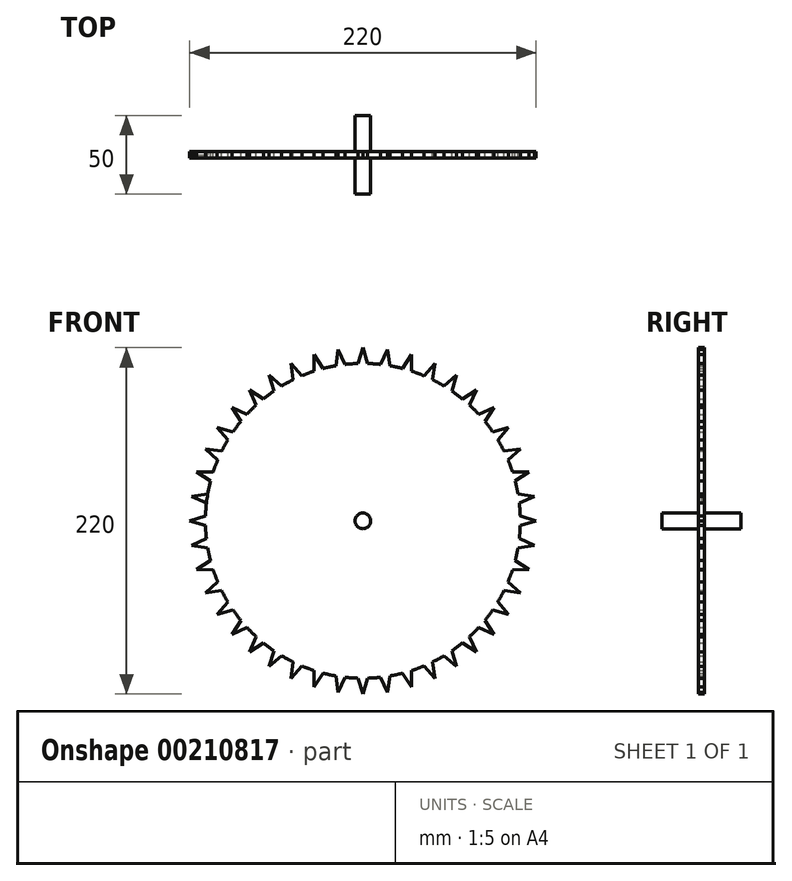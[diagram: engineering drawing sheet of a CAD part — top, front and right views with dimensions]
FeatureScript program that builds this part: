
annotation { "Feature Type Name" : "Feature", "Feature Type Description" : "" }
export const myFeature = defineFeature(function(context is Context, id is Id, definition is map)
    precondition{}
    {
        {
            var Q0;
            Q0=qCreatedBy(makeId("Front.planeOp"),FACE);
            var sketch = newSketch(context, id + "F0", { "sketchPlane" : qUnion([Q0])});
            skArc(sketch, "E0", {"start": v(135, 67.77) * mm, "mid": v(133.09, 71.44) * mm, "end": v(131.03, 75.03) * mm});
            skCircle(sketch, "E1", {"center": v(45.32, 23.52) * mm, "radius": 5 * mm});
            skCircle(sketch, "E2", {"center": v(45.32, 23.52) * mm, "radius": 110 * mm});
            skLineSegment(sketch, "E3", {"start": v(45.32, 123.52) * mm, "end": v(45.32, 133.52) * mm, "construction": true});
            skLineSegment(sketch, "E4", {"start": v(45.32, 133.52) * mm, "end": v(48.32, 123.47) * mm});
            skLineSegment(sketch, "E5.MirrorCS", {"start": v(45.32, 133.52) * mm, "end": v(42.32, 123.47) * mm});
            skLineSegment(sketch, "E6.1.0", {"start": v(59.55, 122.5) * mm, "end": v(60.98, 132.4) * mm, "construction": true});
            skLineSegment(sketch, "E6.1.1", {"start": v(60.98, 132.4) * mm, "end": v(56.58, 122.88) * mm});
            skLineSegment(sketch, "E6.1.2", {"start": v(60.98, 132.4) * mm, "end": v(62.52, 122.03) * mm});
            skLineSegment(sketch, "E6.2.0", {"start": v(73.5, 119.47) * mm, "end": v(76.31, 129.06) * mm, "construction": true});
            skLineSegment(sketch, "E6.2.1", {"start": v(76.31, 129.06) * mm, "end": v(70.6, 120.27) * mm});
            skLineSegment(sketch, "E6.2.2", {"start": v(76.31, 129.06) * mm, "end": v(76.36, 118.58) * mm});
            skLineSegment(sketch, "E6.3.0", {"start": v(86.86, 114.48) * mm, "end": v(91.02, 123.58) * mm, "construction": true});
            skLineSegment(sketch, "E6.3.1", {"start": v(91.02, 123.58) * mm, "end": v(84.12, 115.69) * mm});
            skLineSegment(sketch, "E6.3.2", {"start": v(91.02, 123.58) * mm, "end": v(89.57, 113.2) * mm});
            skLineSegment(sketch, "E6.4.0", {"start": v(99.39, 107.64) * mm, "end": v(104.8, 116.06) * mm, "construction": true});
            skLineSegment(sketch, "E6.4.1", {"start": v(104.8, 116.06) * mm, "end": v(96.84, 109.23) * mm});
            skLineSegment(sketch, "E6.4.2", {"start": v(104.8, 116.06) * mm, "end": v(101.88, 105.98) * mm});
            skLineSegment(sketch, "E6.5.0", {"start": v(110.8, 99.1) * mm, "end": v(117.36, 106.65) * mm, "construction": true});
            skLineSegment(sketch, "E6.5.1", {"start": v(117.36, 106.65) * mm, "end": v(108.51, 101.02) * mm});
            skLineSegment(sketch, "E6.5.2", {"start": v(117.36, 106.65) * mm, "end": v(113.05, 97.1) * mm});
            skLineSegment(sketch, "E6.6.0", {"start": v(120.9, 89) * mm, "end": v(128.45, 95.55) * mm, "construction": true});
            skLineSegment(sketch, "E6.6.1", {"start": v(128.45, 95.55) * mm, "end": v(118.9, 91.24) * mm});
            skLineSegment(sketch, "E6.6.2", {"start": v(128.45, 95.55) * mm, "end": v(122.83, 86.7) * mm});
            skLineSegment(sketch, "E6.7.0", {"start": v(129.45, 77.58) * mm, "end": v(137.86, 82.99) * mm, "construction": true});
            skLineSegment(sketch, "E6.7.1", {"start": v(137.86, 82.99) * mm, "end": v(127.79, 80.08) * mm});
            skLineSegment(sketch, "E6.7.2", {"start": v(137.86, 82.99) * mm, "end": v(131.03, 75.03) * mm});
            skLineSegment(sketch, "E6.8.0", {"start": v(136.28, 65.06) * mm, "end": v(145.38, 69.21) * mm, "construction": true});
            skLineSegment(sketch, "E6.8.1", {"start": v(145.38, 69.21) * mm, "end": v(135, 67.77) * mm});
            skLineSegment(sketch, "E6.8.2", {"start": v(145.38, 69.21) * mm, "end": v(137.49, 62.31) * mm});
            skLineSegment(sketch, "E6.9.0", {"start": v(141.27, 51.7) * mm, "end": v(150.87, 54.5) * mm, "construction": true});
            skLineSegment(sketch, "E6.9.1", {"start": v(150.87, 54.5) * mm, "end": v(140.38, 54.56) * mm});
            skLineSegment(sketch, "E6.9.2", {"start": v(150.87, 54.5) * mm, "end": v(142.07, 48.8) * mm});
            skLineSegment(sketch, "E6.10.0", {"start": v(144.3, 37.75) * mm, "end": v(154.2, 39.17) * mm, "construction": true});
            skLineSegment(sketch, "E6.10.1", {"start": v(154.2, 39.17) * mm, "end": v(143.83, 40.71) * mm});
            skLineSegment(sketch, "E6.10.2", {"start": v(154.2, 39.17) * mm, "end": v(144.69, 34.77) * mm});
            skLineSegment(sketch, "E6.11.0", {"start": v(145.32, 23.52) * mm, "end": v(155.32, 23.52) * mm, "construction": true});
            skLineSegment(sketch, "E6.11.1", {"start": v(155.32, 23.52) * mm, "end": v(145.28, 26.52) * mm});
            skLineSegment(sketch, "E6.11.2", {"start": v(155.32, 23.52) * mm, "end": v(145.28, 20.52) * mm});
            skLineSegment(sketch, "E6.12.0", {"start": v(144.3, 9.29) * mm, "end": v(154.2, 7.86) * mm, "construction": true});
            skLineSegment(sketch, "E6.12.1", {"start": v(154.2, 7.86) * mm, "end": v(144.69, 12.26) * mm});
            skLineSegment(sketch, "E6.12.2", {"start": v(154.2, 7.86) * mm, "end": v(143.83, 6.32) * mm});
            skLineSegment(sketch, "E6.13.0", {"start": v(141.27, -4.66) * mm, "end": v(150.87, -7.47) * mm, "construction": true});
            skLineSegment(sketch, "E6.13.1", {"start": v(150.87, -7.47) * mm, "end": v(142.07, -1.76) * mm});
            skLineSegment(sketch, "E6.13.2", {"start": v(150.87, -7.47) * mm, "end": v(140.38, -7.52) * mm});
            skLineSegment(sketch, "E6.14.0", {"start": v(136.28, -18.02) * mm, "end": v(145.38, -22.18) * mm, "construction": true});
            skLineSegment(sketch, "E6.14.1", {"start": v(145.38, -22.18) * mm, "end": v(137.49, -15.28) * mm});
            skLineSegment(sketch, "E6.14.2", {"start": v(145.38, -22.18) * mm, "end": v(135, -20.73) * mm});
            skLineSegment(sketch, "E6.15.0", {"start": v(129.45, -30.55) * mm, "end": v(137.86, -35.95) * mm, "construction": true});
            skLineSegment(sketch, "E6.15.1", {"start": v(137.86, -35.95) * mm, "end": v(131.03, -28) * mm});
            skLineSegment(sketch, "E6.15.2", {"start": v(137.86, -35.95) * mm, "end": v(127.79, -33.05) * mm});
            skLineSegment(sketch, "E6.16.0", {"start": v(120.9, -41.97) * mm, "end": v(128.45, -48.52) * mm, "construction": true});
            skLineSegment(sketch, "E6.16.1", {"start": v(128.45, -48.52) * mm, "end": v(122.83, -39.67) * mm});
            skLineSegment(sketch, "E6.16.2", {"start": v(128.45, -48.52) * mm, "end": v(118.9, -44.2) * mm});
            skLineSegment(sketch, "E6.17.0", {"start": v(110.8, -52.06) * mm, "end": v(117.36, -59.61) * mm, "construction": true});
            skLineSegment(sketch, "E6.17.1", {"start": v(117.36, -59.61) * mm, "end": v(113.05, -50.06) * mm});
            skLineSegment(sketch, "E6.17.2", {"start": v(117.36, -59.61) * mm, "end": v(108.51, -53.99) * mm});
            skLineSegment(sketch, "E6.18.0", {"start": v(99.39, -60.6) * mm, "end": v(104.8, -69.02) * mm, "construction": true});
            skLineSegment(sketch, "E6.18.1", {"start": v(104.8, -69.02) * mm, "end": v(101.88, -58.95) * mm});
            skLineSegment(sketch, "E6.18.2", {"start": v(104.8, -69.02) * mm, "end": v(96.84, -62.2) * mm});
            skLineSegment(sketch, "E6.19.0", {"start": v(86.86, -67.45) * mm, "end": v(91.02, -76.54) * mm, "construction": true});
            skLineSegment(sketch, "E6.19.1", {"start": v(91.02, -76.54) * mm, "end": v(89.57, -66.16) * mm});
            skLineSegment(sketch, "E6.19.2", {"start": v(91.02, -76.54) * mm, "end": v(84.12, -68.65) * mm});
            skLineSegment(sketch, "E6.20.0", {"start": v(73.5, -72.43) * mm, "end": v(76.31, -82.03) * mm, "construction": true});
            skLineSegment(sketch, "E6.20.1", {"start": v(76.31, -82.03) * mm, "end": v(76.36, -71.54) * mm});
            skLineSegment(sketch, "E6.20.2", {"start": v(76.31, -82.03) * mm, "end": v(70.6, -73.23) * mm});
            skLineSegment(sketch, "E6.21.0", {"start": v(59.55, -75.46) * mm, "end": v(60.98, -85.36) * mm, "construction": true});
            skLineSegment(sketch, "E6.21.1", {"start": v(60.98, -85.36) * mm, "end": v(62.52, -75) * mm});
            skLineSegment(sketch, "E6.21.2", {"start": v(60.98, -85.36) * mm, "end": v(56.58, -75.85) * mm});
            skLineSegment(sketch, "E6.22.0", {"start": v(45.32, -76.48) * mm, "end": v(45.32, -86.48) * mm, "construction": true});
            skLineSegment(sketch, "E6.22.1", {"start": v(45.32, -86.48) * mm, "end": v(48.32, -76.44) * mm});
            skLineSegment(sketch, "E6.22.2", {"start": v(45.32, -86.48) * mm, "end": v(42.32, -76.44) * mm});
            skLineSegment(sketch, "E6.23.0", {"start": v(31.1, -75.46) * mm, "end": v(29.67, -85.36) * mm, "construction": true});
            skLineSegment(sketch, "E6.23.1", {"start": v(29.67, -85.36) * mm, "end": v(34.07, -75.85) * mm});
            skLineSegment(sketch, "E6.23.2", {"start": v(29.67, -85.36) * mm, "end": v(28.13, -75) * mm});
            skLineSegment(sketch, "E6.24.0", {"start": v(17.15, -72.43) * mm, "end": v(14.33, -82.03) * mm, "construction": true});
            skLineSegment(sketch, "E6.24.1", {"start": v(14.33, -82.03) * mm, "end": v(20.04, -73.23) * mm});
            skLineSegment(sketch, "E6.24.2", {"start": v(14.33, -82.03) * mm, "end": v(14.28, -71.54) * mm});
            skLineSegment(sketch, "E6.25.0", {"start": v(3.78, -67.45) * mm, "end": v(-0.37, -76.54) * mm, "construction": true});
            skLineSegment(sketch, "E6.25.1", {"start": v(-0.37, -76.54) * mm, "end": v(6.53, -68.65) * mm});
            skLineSegment(sketch, "E6.25.2", {"start": v(-0.37, -76.54) * mm, "end": v(1.07, -66.16) * mm});
            skLineSegment(sketch, "E6.26.0", {"start": v(-8.74, -60.6) * mm, "end": v(-14.15, -69.02) * mm, "construction": true});
            skLineSegment(sketch, "E6.26.1", {"start": v(-14.15, -69.02) * mm, "end": v(-6.2, -62.2) * mm});
            skLineSegment(sketch, "E6.26.2", {"start": v(-14.15, -69.02) * mm, "end": v(-11.24, -58.95) * mm});
            skLineSegment(sketch, "E6.27.0", {"start": v(-20.16, -52.06) * mm, "end": v(-26.71, -59.61) * mm, "construction": true});
            skLineSegment(sketch, "E6.27.1", {"start": v(-26.71, -59.61) * mm, "end": v(-17.87, -53.99) * mm});
            skLineSegment(sketch, "E6.27.2", {"start": v(-26.71, -59.61) * mm, "end": v(-22.4, -50.06) * mm});
            skLineSegment(sketch, "E6.28.0", {"start": v(-30.25, -41.97) * mm, "end": v(-37.81, -48.52) * mm, "construction": true});
            skLineSegment(sketch, "E6.28.1", {"start": v(-37.81, -48.52) * mm, "end": v(-28.26, -44.2) * mm});
            skLineSegment(sketch, "E6.28.2", {"start": v(-37.81, -48.52) * mm, "end": v(-32.18, -39.67) * mm});
            skLineSegment(sketch, "E6.29.0", {"start": v(-38.8, -30.55) * mm, "end": v(-47.22, -35.95) * mm, "construction": true});
            skLineSegment(sketch, "E6.29.1", {"start": v(-47.22, -35.95) * mm, "end": v(-37.14, -33.05) * mm});
            skLineSegment(sketch, "E6.29.2", {"start": v(-47.22, -35.95) * mm, "end": v(-40.39, -28) * mm});
            skLineSegment(sketch, "E6.anchor1", {"start": v(45.32, 23.52) * mm, "end": v(45.32, 123.52) * mm, "construction": true});
            skLineSegment(sketch, "E6.anchor2", {"start": v(45.32, 23.52) * mm, "end": v(45.32, 123.52) * mm, "construction": true});
            skLineSegment(sketch, "E7.1.30.0", {"start": v(-45.64, -18.02) * mm, "end": v(-54.74, -22.18) * mm, "construction": true});
            skLineSegment(sketch, "E7.3.30.0", {"start": v(-54.74, -22.18) * mm, "end": v(-44.35, -20.73) * mm});
            skLineSegment(sketch, "E7.6.30.0", {"start": v(-54.74, -22.18) * mm, "end": v(-46.85, -15.28) * mm});
            skLineSegment(sketch, "E7.1.31.0", {"start": v(-50.63, -4.66) * mm, "end": v(-60.22, -7.47) * mm, "construction": true});
            skLineSegment(sketch, "E7.3.31.0", {"start": v(-60.22, -7.47) * mm, "end": v(-49.74, -7.52) * mm});
            skLineSegment(sketch, "E7.6.31.0", {"start": v(-60.22, -7.47) * mm, "end": v(-51.43, -1.76) * mm});
            skLineSegment(sketch, "E7.1.32.0", {"start": v(-53.66, 9.29) * mm, "end": v(-63.56, 7.86) * mm, "construction": true});
            skLineSegment(sketch, "E7.3.32.0", {"start": v(-63.56, 7.86) * mm, "end": v(-53.19, 6.32) * mm});
            skLineSegment(sketch, "E7.6.32.0", {"start": v(-63.56, 7.86) * mm, "end": v(-54.04, 12.26) * mm});
            skLineSegment(sketch, "E7.1.33.0", {"start": v(-54.68, 23.52) * mm, "end": v(-64.68, 23.52) * mm, "construction": true});
            skLineSegment(sketch, "E7.3.33.0", {"start": v(-64.68, 23.52) * mm, "end": v(-54.63, 20.52) * mm});
            skLineSegment(sketch, "E7.6.33.0", {"start": v(-64.68, 23.52) * mm, "end": v(-54.63, 26.52) * mm});
            skLineSegment(sketch, "E7.1.34.0", {"start": v(-53.66, 37.75) * mm, "end": v(-63.56, 39.17) * mm, "construction": true});
            skLineSegment(sketch, "E7.3.34.0", {"start": v(-63.56, 39.17) * mm, "end": v(-54.04, 34.77) * mm});
            skLineSegment(sketch, "E7.6.34.0", {"start": v(-63.56, 39.17) * mm, "end": v(-53.19, 40.71) * mm});
            skLineSegment(sketch, "E7.1.35.0", {"start": v(-50.63, 51.7) * mm, "end": v(-60.22, 54.5) * mm, "construction": true});
            skLineSegment(sketch, "E7.3.35.0", {"start": v(-60.22, 54.5) * mm, "end": v(-51.43, 48.8) * mm});
            skLineSegment(sketch, "E7.6.35.0", {"start": v(-60.22, 54.5) * mm, "end": v(-49.74, 54.56) * mm});
            skLineSegment(sketch, "E7.1.36.0", {"start": v(-45.64, 65.06) * mm, "end": v(-54.74, 69.21) * mm, "construction": true});
            skLineSegment(sketch, "E7.3.36.0", {"start": v(-54.74, 69.21) * mm, "end": v(-46.85, 62.31) * mm});
            skLineSegment(sketch, "E7.6.36.0", {"start": v(-54.74, 69.21) * mm, "end": v(-44.35, 67.77) * mm});
            skLineSegment(sketch, "E7.1.37.0", {"start": v(-38.8, 77.58) * mm, "end": v(-47.22, 82.99) * mm, "construction": true});
            skLineSegment(sketch, "E7.3.37.0", {"start": v(-47.22, 82.99) * mm, "end": v(-40.39, 75.03) * mm});
            skLineSegment(sketch, "E7.6.37.0", {"start": v(-47.22, 82.99) * mm, "end": v(-37.14, 80.08) * mm});
            skLineSegment(sketch, "E7.1.38.0", {"start": v(-30.25, 89) * mm, "end": v(-37.81, 95.55) * mm, "construction": true});
            skLineSegment(sketch, "E7.3.38.0", {"start": v(-37.81, 95.55) * mm, "end": v(-32.18, 86.7) * mm});
            skLineSegment(sketch, "E7.6.38.0", {"start": v(-37.81, 95.55) * mm, "end": v(-28.26, 91.24) * mm});
            skLineSegment(sketch, "E7.1.39.0", {"start": v(-20.16, 99.1) * mm, "end": v(-26.71, 106.65) * mm, "construction": true});
            skLineSegment(sketch, "E7.3.39.0", {"start": v(-26.71, 106.65) * mm, "end": v(-22.4, 97.1) * mm});
            skLineSegment(sketch, "E7.6.39.0", {"start": v(-26.71, 106.65) * mm, "end": v(-17.87, 101.02) * mm});
            skLineSegment(sketch, "E7.1.40.0", {"start": v(-8.74, 107.64) * mm, "end": v(-14.15, 116.06) * mm, "construction": true});
            skLineSegment(sketch, "E7.3.40.0", {"start": v(-14.15, 116.06) * mm, "end": v(-11.24, 105.98) * mm});
            skLineSegment(sketch, "E7.6.40.0", {"start": v(-14.15, 116.06) * mm, "end": v(-6.2, 109.23) * mm});
            skLineSegment(sketch, "E7.1.41.0", {"start": v(3.78, 114.48) * mm, "end": v(-0.37, 123.58) * mm, "construction": true});
            skLineSegment(sketch, "E7.3.41.0", {"start": v(-0.37, 123.58) * mm, "end": v(1.07, 113.2) * mm});
            skLineSegment(sketch, "E7.6.41.0", {"start": v(-0.37, 123.58) * mm, "end": v(6.53, 115.69) * mm});
            skLineSegment(sketch, "E7.1.42.0", {"start": v(17.15, 119.47) * mm, "end": v(14.33, 129.06) * mm, "construction": true});
            skLineSegment(sketch, "E7.3.42.0", {"start": v(14.33, 129.06) * mm, "end": v(14.28, 118.58) * mm});
            skLineSegment(sketch, "E7.6.42.0", {"start": v(14.33, 129.06) * mm, "end": v(20.04, 120.27) * mm});
            skLineSegment(sketch, "E7.1.43.0", {"start": v(31.1, 122.5) * mm, "end": v(29.67, 132.4) * mm, "construction": true});
            skLineSegment(sketch, "E7.3.43.0", {"start": v(29.67, 132.4) * mm, "end": v(28.13, 122.03) * mm});
            skLineSegment(sketch, "E7.6.43.0", {"start": v(29.67, 132.4) * mm, "end": v(34.07, 122.88) * mm});
            skArc(sketch, "E8.trimOffspring", {"start": v(127.79, 80.08) * mm, "mid": v(125.38, 83.45) * mm, "end": v(122.83, 86.7) * mm});
            skArc(sketch, "E9.trimOffspring", {"start": v(110.8, 99.1) * mm, "mid": v(106.44, 102.66) * mm, "end": v(101.88, 105.98) * mm});
            skArc(sketch, "E10.trimOffspring", {"start": v(99.39, 107.64) * mm, "mid": v(94.56, 110.56) * mm, "end": v(89.57, 113.2) * mm});
            skArc(sketch, "E11.trimOffspring", {"start": v(86.86, 114.48) * mm, "mid": v(81.67, 116.68) * mm, "end": v(76.36, 118.58) * mm});
            skArc(sketch, "E12.trimOffspring", {"start": v(73.5, 119.47) * mm, "mid": v(68.04, 120.9) * mm, "end": v(62.52, 122.03) * mm});
            skArc(sketch, "E13.trimOffspring", {"start": v(59.55, 122.5) * mm, "mid": v(53.95, 123.15) * mm, "end": v(48.32, 123.47) * mm});
            skArc(sketch, "E14.trimOffspring", {"start": v(45.32, 123.52) * mm, "mid": v(39.68, 123.36) * mm, "end": v(34.07, 122.88) * mm});
            skArc(sketch, "E15.trimOffspring", {"start": v(31.1, 122.5) * mm, "mid": v(25.53, 121.54) * mm, "end": v(20.04, 120.27) * mm});
            skArc(sketch, "E16.trimOffspring", {"start": v(17.15, 119.47) * mm, "mid": v(11.78, 117.73) * mm, "end": v(6.53, 115.69) * mm});
            skArc(sketch, "E17.trimOffspring", {"start": v(3.78, 114.48) * mm, "mid": v(-1.28, 112) * mm, "end": v(-6.2, 109.23) * mm});
            skArc(sketch, "E18.trimOffspring", {"start": v(-8.74, 107.64) * mm, "mid": v(-13.4, 104.46) * mm, "end": v(-17.87, 101.02) * mm});
            skArc(sketch, "E19.trimOffspring", {"start": v(-20.16, 99.1) * mm, "mid": v(-24.32, 95.28) * mm, "end": v(-28.26, 91.24) * mm});
            skArc(sketch, "E20.trimOffspring", {"start": v(-30.25, 89) * mm, "mid": v(-33.82, 84.64) * mm, "end": v(-37.14, 80.08) * mm});
            skArc(sketch, "E21.trimOffspring", {"start": v(-38.8, 77.58) * mm, "mid": v(-41.72, 72.75) * mm, "end": v(-44.35, 67.77) * mm});
            skArc(sketch, "E22.trimOffspring", {"start": v(-45.64, 65.06) * mm, "mid": v(-47.84, 59.87) * mm, "end": v(-49.74, 54.56) * mm});
            skArc(sketch, "E23.trimOffspring", {"start": v(-50.63, 51.7) * mm, "mid": v(-53.44, 39.23) * mm, "end": v(-54.63, 26.52) * mm});
            skArc(sketch, "E24.trimOffspring", {"start": v(-54.68, 23.52) * mm, "mid": v(-54.52, 17.88) * mm, "end": v(-54.04, 12.26) * mm});
            skArc(sketch, "E25.trimOffspring", {"start": v(-53.66, 9.29) * mm, "mid": v(-52.7, 3.73) * mm, "end": v(-51.43, -1.76) * mm});
            skArc(sketch, "E26.trimOffspring", {"start": v(-50.63, -4.66) * mm, "mid": v(-48.89, -10.02) * mm, "end": v(-46.85, -15.28) * mm});
            skArc(sketch, "E27.trimOffspring", {"start": v(-45.64, -18.02) * mm, "mid": v(-43.16, -23.08) * mm, "end": v(-40.39, -28) * mm});
            skArc(sketch, "E28.trimOffspring", {"start": v(-38.8, -30.55) * mm, "mid": v(-35.62, -35.2) * mm, "end": v(-32.18, -39.67) * mm});
            skArc(sketch, "E29.trimOffspring", {"start": v(-30.25, -41.97) * mm, "mid": v(-26.44, -46.12) * mm, "end": v(-22.4, -50.06) * mm});
            skArc(sketch, "E30.trimOffspring", {"start": v(-20.16, -52.06) * mm, "mid": v(-15.8, -55.63) * mm, "end": v(-11.24, -58.95) * mm});
            skArc(sketch, "E31.trimOffspring", {"start": v(-8.74, -60.6) * mm, "mid": v(-3.91, -63.52) * mm, "end": v(1.07, -66.16) * mm});
            skArc(sketch, "E32.trimOffspring", {"start": v(3.78, -67.45) * mm, "mid": v(8.97, -69.64) * mm, "end": v(14.28, -71.54) * mm});
            skArc(sketch, "E33.trimOffspring", {"start": v(17.15, -72.43) * mm, "mid": v(22.6, -73.87) * mm, "end": v(28.13, -75) * mm});
            skArc(sketch, "E34.trimOffspring", {"start": v(31.1, -75.46) * mm, "mid": v(36.7, -76.1) * mm, "end": v(42.32, -76.44) * mm});
            skArc(sketch, "E35.trimOffspring", {"start": v(45.32, -76.48) * mm, "mid": v(50.96, -76.32) * mm, "end": v(56.58, -75.85) * mm});
            skArc(sketch, "E36.trimOffspring", {"start": v(59.55, -75.46) * mm, "mid": v(65.1, -74.5) * mm, "end": v(70.6, -73.23) * mm});
            skArc(sketch, "E37.trimOffspring", {"start": v(73.5, -72.43) * mm, "mid": v(78.86, -70.7) * mm, "end": v(84.12, -68.65) * mm});
            skArc(sketch, "E38.trimOffspring", {"start": v(86.86, -67.45) * mm, "mid": v(91.92, -64.96) * mm, "end": v(96.84, -62.2) * mm});
            skArc(sketch, "E39.trimOffspring", {"start": v(99.39, -60.6) * mm, "mid": v(100.64, -59.79) * mm, "end": v(101.88, -58.95) * mm});
            skArc(sketch, "E40.trimOffspring", {"start": v(110.8, -52.06) * mm, "mid": v(114.96, -48.25) * mm, "end": v(118.9, -44.2) * mm});
            skArc(sketch, "E41.trimOffspring", {"start": v(129.45, -30.55) * mm, "mid": v(130.25, -29.28) * mm, "end": v(131.03, -28) * mm});
            skArc(sketch, "E42.trimOffspring", {"start": v(120.9, -41.97) * mm, "mid": v(124.47, -37.6) * mm, "end": v(127.79, -33.05) * mm});
            skArc(sketch, "E43.trimOffspring", {"start": v(136.28, -18.02) * mm, "mid": v(138.48, -12.83) * mm, "end": v(140.38, -7.52) * mm});
            skArc(sketch, "E44.trimOffspring", {"start": v(141.27, -4.66) * mm, "mid": v(142.7, 0.8) * mm, "end": v(143.83, 6.32) * mm});
            skArc(sketch, "E45.trimOffspring", {"start": v(144.3, 9.29) * mm, "mid": v(144.95, 14.89) * mm, "end": v(145.28, 20.52) * mm});
            skArc(sketch, "E46.trimOffspring", {"start": v(145.32, 23.52) * mm, "mid": v(145.16, 29.16) * mm, "end": v(144.69, 34.77) * mm});
            skArc(sketch, "E47.trimOffspring", {"start": v(144.3, 37.75) * mm, "mid": v(143.34, 43.3) * mm, "end": v(142.07, 48.8) * mm});
            skArc(sketch, "E48.trimOffspring", {"start": v(141.27, 51.7) * mm, "mid": v(139.53, 57.06) * mm, "end": v(137.49, 62.31) * mm});
            skArc(sketch, "E49", {"start": v(131.03, -28) * mm, "mid": v(133.09, -24.4) * mm, "end": v(135, -20.73) * mm});
            skArc(sketch, "E50", {"start": v(118.9, 91.24) * mm, "mid": v(116.03, 94.23) * mm, "end": v(113.05, 97.1) * mm});
            skArc(sketch, "E51", {"start": v(101.88, -58.95) * mm, "mid": v(105.25, -56.54) * mm, "end": v(108.51, -53.99) * mm});
            skSolve(sketch);
        }
        {
            var Q0;
            Q0=makeQuery(id+"F0.imprint","IMPRINT",FACE,{"disambiguationData":[TD([[makeQuery(id+"F0.imprint","IMPRINT",EDGE,{"derivedFrom":sQuery(id+"F0.wireOp",EDGE,"E1")}),1.0]])]});
            extrude(context, id + "F1", {"entities" : qUnion([Q0]), "depth" : 25 * mm, "hasSecondDirection" : true, "secondDirectionOppositeDirection" : true, "secondDirectionDepth" : 25 * mm});
        }
        {
            var Q0;
            Q0=makeQuery(id+"F0.imprint","IMPRINT",FACE,{"disambiguationData":[TD([[makeQuery(id+"F0.imprint","IMPRINT",EDGE,{"derivedFrom":sQuery(id+"F0.wireOp",EDGE,"E0")}),1.0]])]});
            extrude(context, id + "F2", {"entities" : qUnion([Q0]), "operationType" : NewBodyOperationType.ADD, "depth" : 2 * mm, "hasSecondDirection" : true, "secondDirectionOppositeDirection" : true, "secondDirectionDepth" : 2 * mm});
        }
        {
            var Q0;
            {var subQ0=sQuery(id+"F0.wireOp",EDGE,"E7.3.34.0");Q0=makeQuery(id+"F0.imprint","IMPRINT",FACE,{"disambiguationData":[TD([[makeQuery(id+"F0.imprint","IMPRINT",EDGE,{"derivedFrom":subQ0}),1.0]])]});}
            var Q1;
            Q1=makeQuery(id+"F2.opExtrude","CAP_FACE",FACE,{"disambiguationData":[OSD([sQuery(id+"F0.wireOp",EDGE,"E0"),sQuery(id+"F0.wireOp",EDGE,"E1"),sQuery(id+"F0.wireOp",EDGE,"E6.1.1"),sQuery(id+"F0.wireOp",EDGE,"E6.1.2"),sQuery(id+"F0.wireOp",EDGE,"E6.2.1"),sQuery(id+"F0.wireOp",EDGE,"E6.2.2"),sQuery(id+"F0.wireOp",EDGE,"E6.3.1"),sQuery(id+"F0.wireOp",EDGE,"E6.3.2"),sQuery(id+"F0.wireOp",EDGE,"E6.4.1"),sQuery(id+"F0.wireOp",EDGE,"E6.4.2"),sQuery(id+"F0.wireOp",EDGE,"E6.5.1"),sQuery(id+"F0.wireOp",EDGE,"E6.5.2"),sQuery(id+"F0.wireOp",EDGE,"E6.6.1"),sQuery(id+"F0.wireOp",EDGE,"E6.6.2"),sQuery(id+"F0.wireOp",EDGE,"E6.7.1"),sQuery(id+"F0.wireOp",EDGE,"E6.7.2"),sQuery(id+"F0.wireOp",EDGE,"E6.8.1"),sQuery(id+"F0.wireOp",EDGE,"E6.8.2"),sQuery(id+"F0.wireOp",EDGE,"E6.9.1"),sQuery(id+"F0.wireOp",EDGE,"E6.9.2"),sQuery(id+"F0.wireOp",EDGE,"E6.10.1"),sQuery(id+"F0.wireOp",EDGE,"E6.10.2"),sQuery(id+"F0.wireOp",EDGE,"E6.11.1"),sQuery(id+"F0.wireOp",EDGE,"E6.11.2"),sQuery(id+"F0.wireOp",EDGE,"E6.12.1"),sQuery(id+"F0.wireOp",EDGE,"E6.12.2"),sQuery(id+"F0.wireOp",EDGE,"E6.13.1"),sQuery(id+"F0.wireOp",EDGE,"E6.13.2"),sQuery(id+"F0.wireOp",EDGE,"E6.14.1"),sQuery(id+"F0.wireOp",EDGE,"E6.14.2"),sQuery(id+"F0.wireOp",EDGE,"E6.15.1"),sQuery(id+"F0.wireOp",EDGE,"E6.15.2"),sQuery(id+"F0.wireOp",EDGE,"E6.16.1"),sQuery(id+"F0.wireOp",EDGE,"E6.16.2"),sQuery(id+"F0.wireOp",EDGE,"E6.17.1"),sQuery(id+"F0.wireOp",EDGE,"E6.17.2"),sQuery(id+"F0.wireOp",EDGE,"E6.18.1"),sQuery(id+"F0.wireOp",EDGE,"E6.18.2"),sQuery(id+"F0.wireOp",EDGE,"E6.19.1"),sQuery(id+"F0.wireOp",EDGE,"E6.19.2"),sQuery(id+"F0.wireOp",EDGE,"E6.20.1"),sQuery(id+"F0.wireOp",EDGE,"E6.20.2"),sQuery(id+"F0.wireOp",EDGE,"E6.21.1"),sQuery(id+"F0.wireOp",EDGE,"E6.21.2"),sQuery(id+"F0.wireOp",EDGE,"E6.22.1"),sQuery(id+"F0.wireOp",EDGE,"E6.22.2"),sQuery(id+"F0.wireOp",EDGE,"E6.23.1"),sQuery(id+"F0.wireOp",EDGE,"E6.23.2"),sQuery(id+"F0.wireOp",EDGE,"E6.24.1"),sQuery(id+"F0.wireOp",EDGE,"E6.24.2"),sQuery(id+"F0.wireOp",EDGE,"E6.25.1"),sQuery(id+"F0.wireOp",EDGE,"E6.25.2"),sQuery(id+"F0.wireOp",EDGE,"E6.26.1"),sQuery(id+"F0.wireOp",EDGE,"E6.26.2"),sQuery(id+"F0.wireOp",EDGE,"E6.27.1"),sQuery(id+"F0.wireOp",EDGE,"E6.27.2"),sQuery(id+"F0.wireOp",EDGE,"E6.28.1"),sQuery(id+"F0.wireOp",EDGE,"E6.28.2"),sQuery(id+"F0.wireOp",EDGE,"E6.29.1"),sQuery(id+"F0.wireOp",EDGE,"E6.29.2"),sQuery(id+"F0.wireOp",EDGE,"E7.3.30.0"),sQuery(id+"F0.wireOp",EDGE,"E7.6.30.0"),sQuery(id+"F0.wireOp",EDGE,"E7.3.31.0"),sQuery(id+"F0.wireOp",EDGE,"E7.6.31.0"),sQuery(id+"F0.wireOp",EDGE,"E7.3.32.0"),sQuery(id+"F0.wireOp",EDGE,"E7.6.32.0"),sQuery(id+"F0.wireOp",EDGE,"E7.3.33.0"),sQuery(id+"F0.wireOp",EDGE,"E7.6.33.0"),sQuery(id+"F0.wireOp",EDGE,"E7.3.35.0"),sQuery(id+"F0.wireOp",EDGE,"E7.6.35.0"),sQuery(id+"F0.wireOp",EDGE,"E7.3.36.0"),sQuery(id+"F0.wireOp",EDGE,"E7.6.36.0"),sQuery(id+"F0.wireOp",EDGE,"E7.3.37.0"),sQuery(id+"F0.wireOp",EDGE,"E7.6.37.0"),sQuery(id+"F0.wireOp",EDGE,"E7.3.38.0"),sQuery(id+"F0.wireOp",EDGE,"E7.6.38.0"),sQuery(id+"F0.wireOp",EDGE,"E7.3.39.0"),sQuery(id+"F0.wireOp",EDGE,"E7.6.39.0"),sQuery(id+"F0.wireOp",EDGE,"E7.3.40.0"),sQuery(id+"F0.wireOp",EDGE,"E7.6.40.0"),sQuery(id+"F0.wireOp",EDGE,"E7.3.41.0"),sQuery(id+"F0.wireOp",EDGE,"E7.6.41.0"),sQuery(id+"F0.wireOp",EDGE,"E7.3.42.0"),sQuery(id+"F0.wireOp",EDGE,"E7.6.42.0"),sQuery(id+"F0.wireOp",EDGE,"E7.3.43.0"),sQuery(id+"F0.wireOp",EDGE,"E7.6.43.0"),sQuery(id+"F0.wireOp",EDGE,"E5.MirrorCS"),sQuery(id+"F0.wireOp",EDGE,"E4"),sQuery(id+"F0.wireOp",EDGE,"E8.trimOffspring"),sQuery(id+"F0.wireOp",EDGE,"E9.trimOffspring"),sQuery(id+"F0.wireOp",EDGE,"E10.trimOffspring"),sQuery(id+"F0.wireOp",EDGE,"E11.trimOffspring"),sQuery(id+"F0.wireOp",EDGE,"E12.trimOffspring"),sQuery(id+"F0.wireOp",EDGE,"E13.trimOffspring"),sQuery(id+"F0.wireOp",EDGE,"E14.trimOffspring"),sQuery(id+"F0.wireOp",EDGE,"E15.trimOffspring"),sQuery(id+"F0.wireOp",EDGE,"E16.trimOffspring"),sQuery(id+"F0.wireOp",EDGE,"E17.trimOffspring"),sQuery(id+"F0.wireOp",EDGE,"E18.trimOffspring"),sQuery(id+"F0.wireOp",EDGE,"E19.trimOffspring"),sQuery(id+"F0.wireOp",EDGE,"E20.trimOffspring"),sQuery(id+"F0.wireOp",EDGE,"E21.trimOffspring"),sQuery(id+"F0.wireOp",EDGE,"E22.trimOffspring"),sQuery(id+"F0.wireOp",EDGE,"E23.trimOffspring"),sQuery(id+"F0.wireOp",EDGE,"E24.trimOffspring"),sQuery(id+"F0.wireOp",EDGE,"E25.trimOffspring"),sQuery(id+"F0.wireOp",EDGE,"E26.trimOffspring"),sQuery(id+"F0.wireOp",EDGE,"E27.trimOffspring"),sQuery(id+"F0.wireOp",EDGE,"E28.trimOffspring"),sQuery(id+"F0.wireOp",EDGE,"E29.trimOffspring"),sQuery(id+"F0.wireOp",EDGE,"E30.trimOffspring"),sQuery(id+"F0.wireOp",EDGE,"E31.trimOffspring"),sQuery(id+"F0.wireOp",EDGE,"E32.trimOffspring"),sQuery(id+"F0.wireOp",EDGE,"E33.trimOffspring"),sQuery(id+"F0.wireOp",EDGE,"E34.trimOffspring"),sQuery(id+"F0.wireOp",EDGE,"E35.trimOffspring"),sQuery(id+"F0.wireOp",EDGE,"E36.trimOffspring"),sQuery(id+"F0.wireOp",EDGE,"E37.trimOffspring"),sQuery(id+"F0.wireOp",EDGE,"E38.trimOffspring"),sQuery(id+"F0.wireOp",EDGE,"E40.trimOffspring"),sQuery(id+"F0.wireOp",EDGE,"E42.trimOffspring"),sQuery(id+"F0.wireOp",EDGE,"E43.trimOffspring"),sQuery(id+"F0.wireOp",EDGE,"E44.trimOffspring"),sQuery(id+"F0.wireOp",EDGE,"E45.trimOffspring"),sQuery(id+"F0.wireOp",EDGE,"E46.trimOffspring"),sQuery(id+"F0.wireOp",EDGE,"E47.trimOffspring"),sQuery(id+"F0.wireOp",EDGE,"E48.trimOffspring"),sQuery(id+"F0.wireOp",EDGE,"E49"),sQuery(id+"F0.wireOp",EDGE,"E50"),sQuery(id+"F0.wireOp",EDGE,"E51")])],"isStart":true});
            extrude(context, id + "F3", {"entities" : qUnion([Q0]), "operationType" : NewBodyOperationType.ADD, "endBound" : BoundingType.UP_TO_SURFACE, "oppositeDirection" : true, "depth" : 25 * mm, "endBoundEntityFace" : qUnion([Q1]), "offsetDistance" : 25 * mm});
        }
    });
